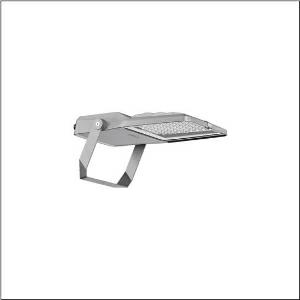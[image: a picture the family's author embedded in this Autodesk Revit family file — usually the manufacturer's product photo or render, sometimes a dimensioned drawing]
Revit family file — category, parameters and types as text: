
# Revit family: floodlight_fl_21_iq_mini___rs12_5xa7772d4b1a_8fae
name_source: partatom
category: Lighting Fixtures
units: mm (PartAtom-declared; Revit-internal decimal feet)

## family parameters
Cut with Voids When Loaded = No
Host = Face
Light Source = No
Part Type = Normal
Room Calculation Point = No
Round Connector Dimension = Use Diameter
Shared = No

## types (1)
- --- (1 x LED, 18810 lm, 143 W, 4000K)
    Apparent Load = 143 VA
    CIE Flux Codes = 79 92 99 100 100
    Color Rendering = 70
    Color Temperature = 4000K
    Default Elevation = 1800 mm
    Description = Floodlight FL 21 iQ mini, floodlight, primary light control with lens, of PMMA, primary optical cover: protective disc, of toughened safety glass, transparent, light distribution: RS12, light emission: direct distribution, installation type: surface-mounted, lamps: LED, High Power LED, rated values: 18.810lm | 143W | 131,5lm/W (begin service life); end service life: 18.810lm | 151,6W; at 50% lumin. flux: 9.405lm | 60,8W | 154,7lm/W, colour temperature: 4000K, colour rendering: CRI > 70, light colour: 740, light setting 1 begin service life: 100% | 18.810lm | 143W | 131,5lm/W | 4.000K, light setting 1 end service life: 151,6W, further light settings possible, control: Street-Remote, Auto-Match, Temp-Guard, Night-Set, Smart-Wire, Desk-Remote (wireless, voltage-free reading and setting of iQ features in the workshop via application-optimized NFC function/RFID function), optimised constant luminous flux control (CLO 2.0), pre-setting: linear dimming characteristic, with terminal, 6-pole, mains connection: 220..240V, AC, 50/60Hz, luminaire housing, of diecast aluminium, powder-coated, SITECO metallic grey (DB 702S), corrosivity category C5 mid according to DIN EN ISO 12944suitable for swimming poolschlorine-resistant, sealing non-destructively replaceable, mounting bracket, of steel, galvanised, powder-coated, SITECO metallic grey (DB 702S), protection rating (complete): IP66, insulation class (complete): insulation class II (safety insulation), certification: CE, ENEC, VDE, protection symbol: D, impact resistance: IK08, permissible operating ambient temperature: -40..+40°C, permissible operating ambient temperature for outdoor applications: -40..+50°C, standard: DIN EN 12944, LABS conformity tested according to VDMA 24364:2018-05, packaging unit: 1 piece

Light Distribution: RS12
    Height = 70 mm
    Lamp = 1 x LED
    Lamp Light Flux = 18810 lm
    Lamp Power = 143 W
    Lamp count = 1
    Length = 485 mm
    Luminous efficacy = 132 lm/W
    Manufacturer = Siteco
    ModVariant = No
    Model = 5XA7772D4B1A
    Number of Poles = 1
    OnlyDefault = Yes
    Power Factor = 1
    Product Name = Floodlight FL 21 iQ mini | RS12
    Product group = floodlight | pylon annexe
    ProductGroupID = 6201
    Protection Class = Protection class II
    Protection Degree = IP 66
    RLX_Detail_Level = 1
    RLX_Emergency_Light_Flux = 0 lm
    RLX_Emergency_Type = 0
    RLX_Emergency_Type_DB = No
    RlxData = <blob elided: 91517 chars, md5=7fe7d680>
    Socket = socket
    Standby Power = 0 W
    System Light Flux = 18810 lm
    System Power = 143 W
    Type Comments = factory setting: luminous flux: 100 % | dim-lin: 254 | 730 mA
    Type Image = l_1006845.jpg
    URL = http://relux.com
    VarID = @adj_166777
    Voltage = 0 V
    Weight = 0.00 kg
    Width = 337 mm

## geometry (parser evidence)
native form markers: Blend x4, Sweep x14
no freeform markers — native parametric forms only
